# Revit family: GRAS_SWSP_N2
name_source: partatom
category: Osprzęt hydrauliczny
revit_build: Autodesk Revit 2018 (Build: 20190510_1515(x64)
units: mm (PartAtom-declared; Revit-internal decimal feet)

## family parameters
Obiekt nadrzędny = Powierzchnia
Punkt obliczania pomieszczeń = Nie
Tnij formami wycięć po wczytaniu = Nie
Typ części = Normalny
Współdzielony = Nie
Wymiar okrągłego złącza = Użyj średnicy

## types (2) — shared parameters
Cabinet depth = 220 mm  [stored 0.721785 ft]
Cabinet height = 450 mm  [stored 1.47638 ft]
Cabinet width = 500 mm  [stored 1.64042 ft]
D1 = 100 mm  [stored 0.328084 ft]
DN = 52 mm
Flow = 240.0 L/s
H1 = 120 mm  [stored 0.393701 ft]
K Factor = 42
Opis = https://gras.pl
Producent = GRAS PPPH
URL = http://www.gras.pl
zero-valued in all types: Domyślna rzędna

## per-type parameters (varying)
| type | Cabinet material |
| SWSP-N2, RAL9010 | DC01, RAL9010 |
| SWSP-N2, RAL3000 | DC01, RAL3000 |

note: column(s) folded — value = type name in every type: Model

note: [stored X ft] marks values corroborated as IEEE doubles in the binary element streams (Revit-internal decimal feet)

## geometry (parser evidence)
native form markers: Blend x8
no freeform markers — native parametric forms only
